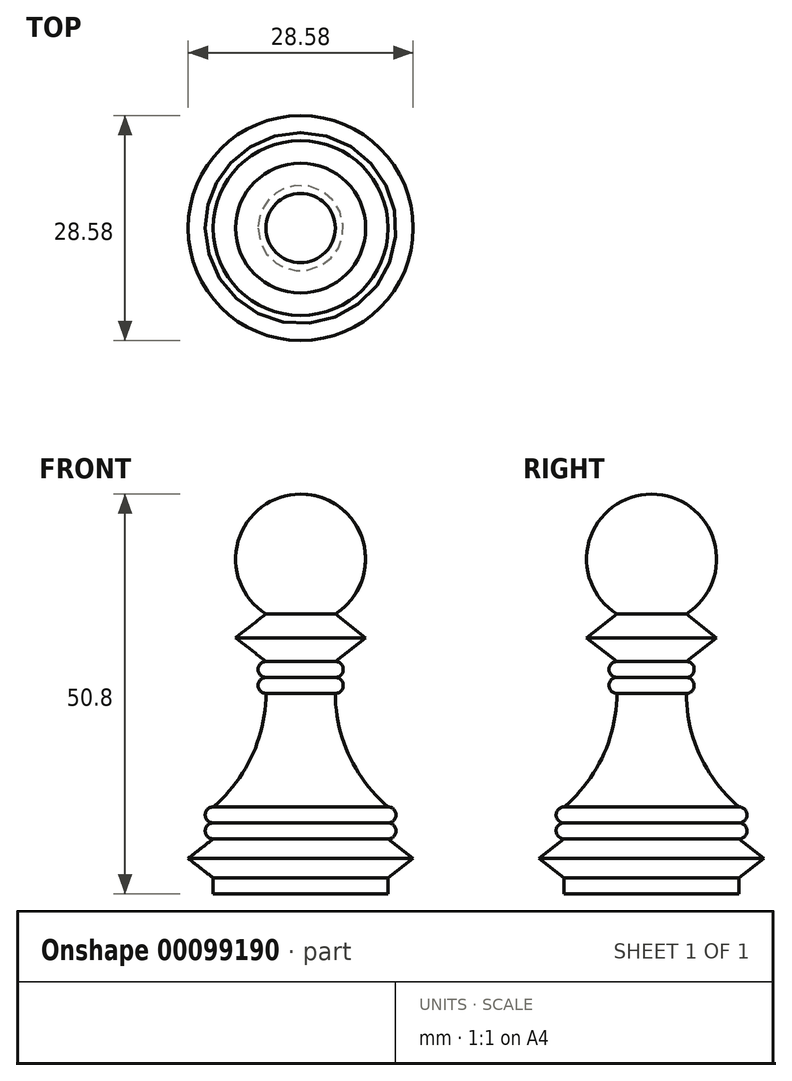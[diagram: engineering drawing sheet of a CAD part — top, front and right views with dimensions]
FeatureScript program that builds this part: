
annotation { "Feature Type Name" : "Feature", "Feature Type Description" : "" }
export const myFeature = defineFeature(function(context is Context, id is Id, definition is map)
    precondition{}
    {
        {
            var Q0;
            Q0=qCreatedBy(makeId("Front.planeOp"),FACE);
            var sketch = newSketch(context, id + "F0", { "sketchPlane" : qUnion([Q0])});
            skLineSegment(sketch, "E0", {"start": v(0, 0) * mm, "end": v(11.11, 0) * mm});
            skLineSegment(sketch, "E1", {"start": v(11.11, 0) * mm, "end": v(11.11, 2.03) * mm});
            skLineSegment(sketch, "E2", {"start": v(11.11, 2.03) * mm, "end": v(14.29, 4.51) * mm});
            skLineSegment(sketch, "E3", {"start": v(14.29, 4.51) * mm, "end": v(11.11, 7) * mm});
            skLineSegment(sketch, "E4", {"start": v(0, 0) * mm, "end": v(0, 50.8) * mm});
            skArc(sketch, "E5", {"start": v(0, 50.8) * mm, "mid": v(7.93, 44.83) * mm, "end": v(4.4, 35.56) * mm});
            skLineSegment(sketch, "E6", {"start": v(4.4, 35.56) * mm, "end": v(8.26, 32.55) * mm});
            skLineSegment(sketch, "E7", {"start": v(8.26, 32.55) * mm, "end": v(4.4, 29.54) * mm});
            skArc(sketch, "E8", {"start": v(4.4, 27.5) * mm, "mid": v(5.42, 28.52) * mm, "end": v(4.4, 29.54) * mm});
            skArc(sketch, "E9", {"start": v(4.4, 25.47) * mm, "mid": v(5.42, 26.49) * mm, "end": v(4.4, 27.5) * mm});
            skArc(sketch, "E10", {"start": v(11.11, 7) * mm, "mid": v(12.13, 8) * mm, "end": v(11.11, 9.03) * mm});
            skArc(sketch, "E11", {"start": v(11.11, 9.03) * mm, "mid": v(12.13, 10.04) * mm, "end": v(11.11, 11.06) * mm});
            skArc(sketch, "E12", {"start": v(4.4, 25.47) * mm, "mid": v(6.18, 17.53) * mm, "end": v(11.11, 11.06) * mm});
            skLineSegment(sketch, "E13", {"start": v(11.11, 7) * mm, "end": v(5.55, 7) * mm, "construction": true});
            skLineSegment(sketch, "E14", {"start": v(11.11, 9.03) * mm, "end": v(6.48, 9.03) * mm, "construction": true});
            skLineSegment(sketch, "E15", {"start": v(4.4, 29.54) * mm, "end": v(2.07, 29.54) * mm, "construction": true});
            skLineSegment(sketch, "E16", {"start": v(4.4, 27.5) * mm, "end": v(2.15, 27.5) * mm, "construction": true});
            skSolve(sketch);
        }
        {
            var Q0;
            Q0=qSketchRegion(id+"F0",true);
            var Q1;
            Q1=sQuery(id+"F0.wireOp",EDGE,"E4");
            revolve(context, id + "F1", {"entities" : qUnion([Q0]), "axis" : qUnion([Q1]), "revolveType" : RevolveType.FULL});
        }
    });
